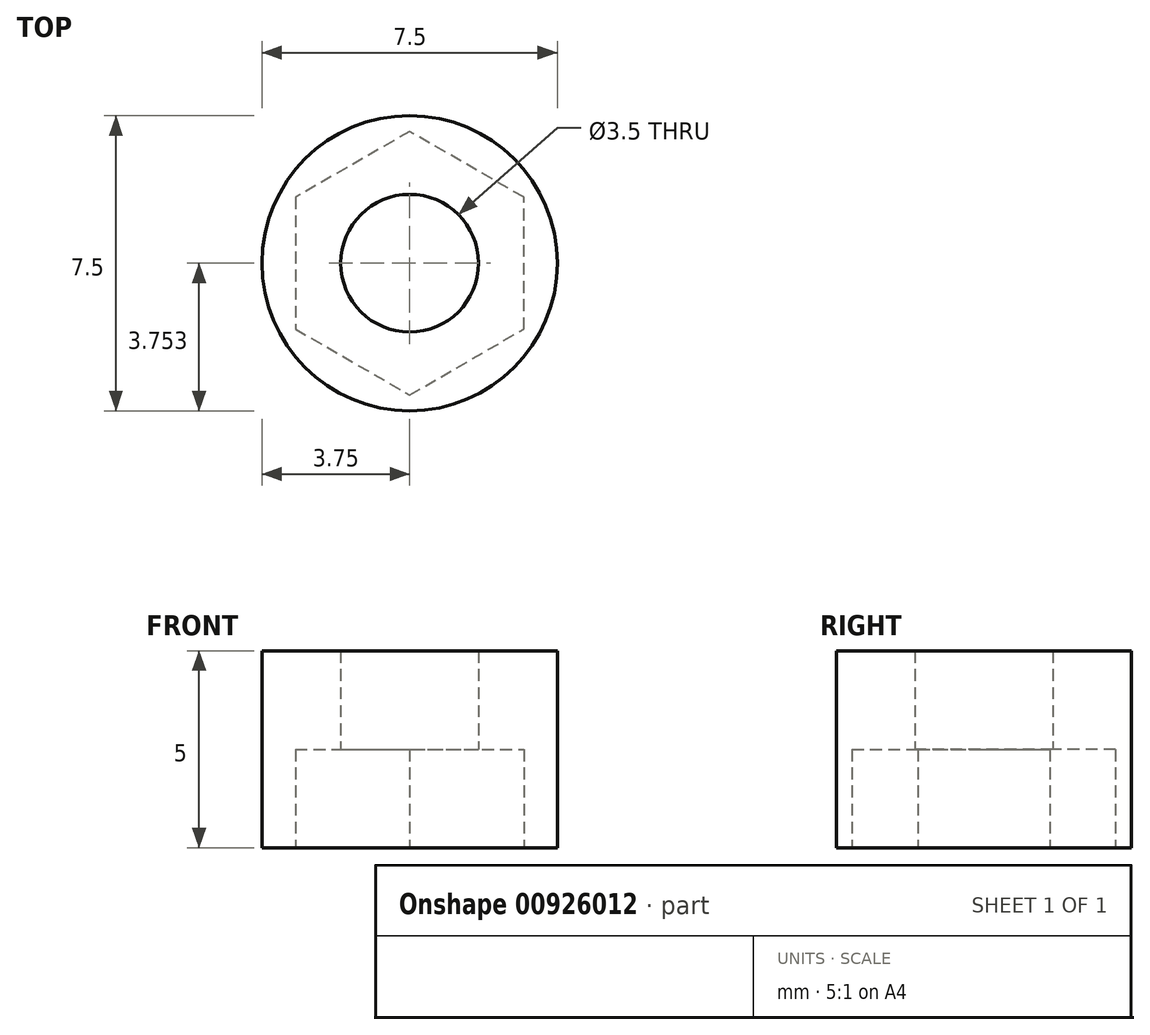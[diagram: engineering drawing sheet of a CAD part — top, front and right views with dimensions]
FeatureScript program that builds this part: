
annotation { "Feature Type Name" : "Feature", "Feature Type Description" : "" }
export const myFeature = defineFeature(function(context is Context, id is Id, definition is map)
    precondition{}
    {
        {
            var Q0;
            Q0=qCreatedBy(makeId("Top.planeOp"),FACE);
            var sketch = newSketch(context, id + "F0", { "sketchPlane" : qUnion([Q0])});
            skCircle(sketch, "E0", {"center": v(56.98, -33.04) * mm, "radius": 3.75 * mm});
            skCircle(sketch, "E1", {"center": v(56.98, -33.04) * mm, "radius": 1.75 * mm});
            skSolve(sketch);
        }
        {
            var Q0;
            Q0=qSketchRegion(id+"F0",true);
            extrude(context, id + "F1", {"entities" : qUnion([Q0]), "depth" : 3.8 * mm, "offsetDistance" : 25 * mm});
        }
        {
            var Q0;
            Q0=makeQuery(id+"F1.opExtrude","CAP_FACE",FACE,{"disambiguationData":[OSD([sQuery(id+"F0.wireOp",EDGE,"E0")])],"isStart":true});
            var sketch = newSketch(context, id + "F2", { "sketchPlane" : qUnion([Q0])});
            skCircle(sketch, "E2.cCircle", {"center": v(56.98, 33.04) * mm, "radius": 2.9 * mm, "construction": true});
            skLineSegment(sketch, "E2.0", {"start": v(59.88, 34.71) * mm, "end": v(59.88, 31.36) * mm});
            skLineSegment(sketch, "E2.1", {"start": v(59.88, 31.36) * mm, "end": v(56.98, 29.69) * mm});
            skLineSegment(sketch, "E2.2", {"start": v(56.98, 29.69) * mm, "end": v(54.08, 31.36) * mm});
            skLineSegment(sketch, "E2.3", {"start": v(54.08, 31.36) * mm, "end": v(54.08, 34.71) * mm});
            skLineSegment(sketch, "E2.4", {"start": v(54.08, 34.71) * mm, "end": v(56.98, 36.39) * mm});
            skLineSegment(sketch, "E2.5", {"start": v(56.98, 36.39) * mm, "end": v(59.88, 34.71) * mm});
            skPoint(sketch, "E2.0.midPoint", {"position": v(59.88, 33.04) * mm});
            skSolve(sketch);
        }
        {
            var Q0;
            Q0=qSketchRegion(id+"F2",true);
            extrude(context, id + "F3", {"entities" : qUnion([Q0]), "operationType" : NewBodyOperationType.REMOVE, "oppositeDirection" : true, "depth" : 2.5 * mm, "offsetDistance" : 25 * mm});
        }
        {
            var Q0;
            Q0=makeQuery(id+"F1.opExtrude","CAP_FACE",FACE,{"disambiguationData":[OSD([sQuery(id+"F0.wireOp",EDGE,"E0"),sQuery(id+"F0.wireOp",EDGE,"E1")])],"isStart":false});
            extrude(context, id + "F4", {"entities" : qUnion([Q0]), "operationType" : NewBodyOperationType.ADD, "depth" : 1.2 * mm, "offsetDistance" : 25 * mm});
        }
    });
